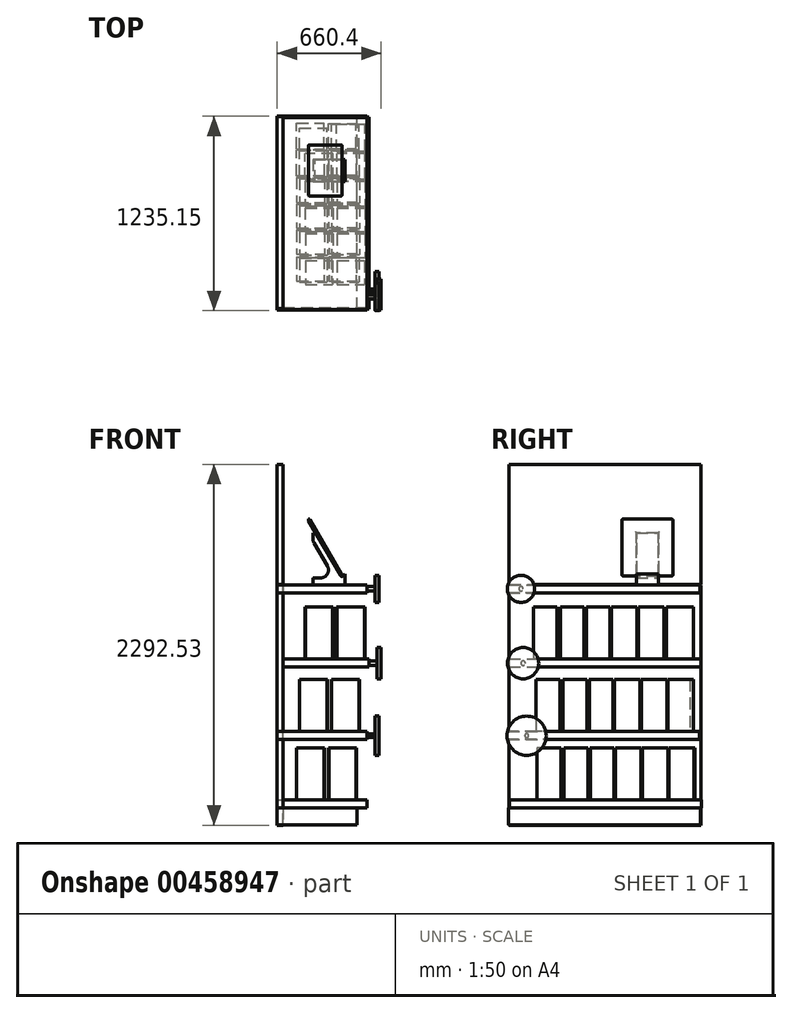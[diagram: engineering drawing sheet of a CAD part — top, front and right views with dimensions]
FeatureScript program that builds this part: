
annotation { "Feature Type Name" : "Feature", "Feature Type Description" : "" }
export const myFeature = defineFeature(function(context is Context, id is Id, definition is map)
    precondition{}
    {
        {
            var Q0;
            Q0=qCreatedBy(makeId("Right.planeOp"),FACE);
            var sketch = newSketch(context, id + "F0", { "sketchPlane" : qUnion([Q0])});
            skLineSegment(sketch, "E0.bottom", {"start": v(227.6, 704.3) * mm, "end": v(1446.8, 704.3) * mm});
            skLineSegment(sketch, "E0.top", {"start": v(227.6, -57.7) * mm, "end": v(1446.8, -57.7) * mm});
            skLineSegment(sketch, "E0.left", {"start": v(227.6, 704.3) * mm, "end": v(227.6, -57.7) * mm});
            skLineSegment(sketch, "E0.right", {"start": v(1446.8, 704.3) * mm, "end": v(1446.8, -57.7) * mm});
            skSolve(sketch);
        }
        {
            var Q0;
            Q0 = qSketchRegion(id + "F0", true);
            extrude(context, id + "F1", {"entities" : qUnion([Q0]), "depth" : 38.1 * mm, "offsetDistance" : 25.4 * mm});
        }
        {
            var Q0;
            Q0=qCreatedBy(makeId("Right.planeOp"),FACE);
            var sketch = newSketch(context, id + "F2", { "sketchPlane" : qUnion([Q0])});
            skLineSegment(sketch, "E1.bottom", {"start": v(225.61, -64.23) * mm, "end": v(1444.81, -64.23) * mm});
            skLineSegment(sketch, "E1.top", {"start": v(225.61, -1588.23) * mm, "end": v(1444.81, -1588.23) * mm});
            skLineSegment(sketch, "E1.left", {"start": v(225.61, -64.23) * mm, "end": v(225.61, -1588.23) * mm});
            skLineSegment(sketch, "E1.right", {"start": v(1444.81, -64.23) * mm, "end": v(1444.81, -1588.23) * mm});
            skSolve(sketch);
        }
        {
            var Q0;
            Q0 = qSketchRegion(id + "F2", true);
            extrude(context, id + "F3", {"entities" : qUnion([Q0]), "depth" : 38.1 * mm, "offsetDistance" : 25.4 * mm});
        }
        {
            var Q0;
            Q0=qCreatedBy(makeId("Right.planeOp"),FACE);
            var sketch = newSketch(context, id + "F4", { "sketchPlane" : qUnion([Q0])});
            skLineSegment(sketch, "E2.bottom", {"start": v(221.35, -62.55) * mm, "end": v(1440.55, -62.55) * mm});
            skLineSegment(sketch, "E2.top", {"start": v(221.35, -113.35) * mm, "end": v(1440.55, -113.35) * mm});
            skLineSegment(sketch, "E2.left", {"start": v(221.35, -62.55) * mm, "end": v(221.35, -113.35) * mm});
            skLineSegment(sketch, "E2.right", {"start": v(1440.55, -62.55) * mm, "end": v(1440.55, -113.35) * mm});
            skSolve(sketch);
        }
        {
            var Q0;
            Q0 = qSketchRegion(id + "F4", true);
            extrude(context, id + "F5", {"entities" : qUnion([Q0]), "operationType" : NewBodyOperationType.ADD, "depth" : 571.5 * mm, "offsetDistance" : 25.4 * mm});
        }
        {
            var Q0;
            Q0=makeQuery(id+"F3.opExtrude","CAP_FACE",FACE,{"disambiguationData":[OSD([sQuery(id+"F2.wireOp",EDGE,"E1.bottom"),sQuery(id+"F2.wireOp",EDGE,"E1.top"),sQuery(id+"F2.wireOp",EDGE,"E1.left"),sQuery(id+"F2.wireOp",EDGE,"E1.right")])],"isStart":false});
            var sketch = newSketch(context, id + "F6", { "sketchPlane" : qUnion([Q0])});
            skLineSegment(sketch, "E3.bottom", {"start": v(225.68, -532.06) * mm, "end": v(1444.88, -532.06) * mm});
            skLineSegment(sketch, "E3.top", {"start": v(225.68, -582.86) * mm, "end": v(1444.88, -582.86) * mm});
            skLineSegment(sketch, "E3.left", {"start": v(225.68, -532.06) * mm, "end": v(225.68, -582.86) * mm});
            skLineSegment(sketch, "E3.right", {"start": v(1444.88, -532.06) * mm, "end": v(1444.88, -582.86) * mm});
            skSolve(sketch);
        }
        {
            var Q0;
            Q0 = qSketchRegion(id + "F6", true);
            extrude(context, id + "F7", {"entities" : qUnion([Q0]), "operationType" : NewBodyOperationType.ADD, "depth" : 546.1 * mm, "offsetDistance" : 25.4 * mm});
        }
        {
            var Q0;
            Q0=qCreatedBy(makeId("Right.planeOp"),FACE);
            var sketch = newSketch(context, id + "F8", { "sketchPlane" : qUnion([Q0])});
            skLineSegment(sketch, "E4.bottom", {"start": v(218, -992.74) * mm, "end": v(1437.2, -992.74) * mm});
            skLineSegment(sketch, "E4.top", {"start": v(218, -1043.54) * mm, "end": v(1437.2, -1043.54) * mm});
            skLineSegment(sketch, "E4.left", {"start": v(218, -992.74) * mm, "end": v(218, -1043.54) * mm});
            skLineSegment(sketch, "E4.right", {"start": v(1437.2, -992.74) * mm, "end": v(1437.2, -1043.54) * mm});
            skSolve(sketch);
        }
        {
            var Q0;
            Q0 = qSketchRegion(id + "F8", true);
            var Q1;
            Q1 = qSketchRegion(id + "F4", true);
            extrude(context, id + "F9", {"entities" : qUnion([Q0, Q1]), "operationType" : NewBodyOperationType.ADD, "depth" : 571.5 * mm, "offsetDistance" : 25.4 * mm});
        }
        {
            var Q0;
            Q0=qCreatedBy(makeId("Right.planeOp"),FACE);
            var sketch = newSketch(context, id + "F10", { "sketchPlane" : qUnion([Q0])});
            skLineSegment(sketch, "E5.bottom", {"start": v(229.96, -1426.88) * mm, "end": v(1449.16, -1426.88) * mm});
            skLineSegment(sketch, "E5.top", {"start": v(229.96, -1477.68) * mm, "end": v(1449.16, -1477.68) * mm});
            skLineSegment(sketch, "E5.left", {"start": v(229.96, -1426.88) * mm, "end": v(229.96, -1477.68) * mm});
            skLineSegment(sketch, "E5.right", {"start": v(1449.16, -1426.88) * mm, "end": v(1449.16, -1477.68) * mm});
            skSolve(sketch);
        }
        {
            var Q0;
            Q0 = qSketchRegion(id + "F10", true);
            extrude(context, id + "F11", {"entities" : qUnion([Q0]), "operationType" : NewBodyOperationType.ADD, "depth" : 571.5 * mm, "offsetDistance" : 25.4 * mm});
        }
        {
            var Q0;
            Q0=qCreatedBy(makeId("Right.planeOp"),FACE);
            var sketch = newSketch(context, id + "F12", { "sketchPlane" : qUnion([Q0])});
            skLineSegment(sketch, "E6.bottom", {"start": v(222.75, -1478.96) * mm, "end": v(1441.83, -1478.96) * mm});
            skLineSegment(sketch, "E6.top", {"start": v(222.75, -1587.43) * mm, "end": v(1441.83, -1587.43) * mm});
            skLineSegment(sketch, "E6.left", {"start": v(222.75, -1478.96) * mm, "end": v(222.75, -1587.43) * mm});
            skLineSegment(sketch, "E6.right", {"start": v(1441.83, -1478.96) * mm, "end": v(1441.83, -1587.43) * mm});
            skSolve(sketch);
        }
        {
            var Q0;
            Q0 = qSketchRegion(id + "F12", true);
            extrude(context, id + "F13", {"entities" : qUnion([Q0]), "operationType" : NewBodyOperationType.ADD, "depth" : 508 * mm, "offsetDistance" : 25.4 * mm});
        }
        {
            var Q0;
            Q0=makeQuery(id+"F5.opExtrude","CAP_FACE",FACE,{"disambiguationData":[OSD([sQuery(id+"F4.wireOp",EDGE,"E2.bottom"),sQuery(id+"F4.wireOp",EDGE,"E2.top"),sQuery(id+"F4.wireOp",EDGE,"E2.left"),sQuery(id+"F4.wireOp",EDGE,"E2.right")])],"isStart":false});
            var sketch = newSketch(context, id + "F14", { "sketchPlane" : qUnion([Q0])});
            skCircle(sketch, "E7", {"center": v(302.83, -86.73) * mm, "radius": 13.67 * mm});
            skSolve(sketch);
        }
        {
            var Q0;
            Q0 = qSketchRegion(id + "F14", true);
            extrude(context, id + "F15", {"entities" : qUnion([Q0]), "operationType" : NewBodyOperationType.ADD, "depth" : 50.8 * mm, "offsetDistance" : 25.4 * mm});
        }
        {
            var Q0;
            Q0=makeQuery(id+"F15.opExtrude","CAP_FACE",FACE,{"disambiguationData":[OSD([sQuery(id+"F14.wireOp",EDGE,"E7")])],"isStart":false});
            var sketch = newSketch(context, id + "F16", { "sketchPlane" : qUnion([Q0])});
            skCircle(sketch, "E8", {"center": v(302.83, -86.73) * mm, "radius": 86.26 * mm});
            skSolve(sketch);
        }
        {
            var Q0;
            Q0 = qSketchRegion(id + "F16", true);
            extrude(context, id + "F17", {"entities" : qUnion([Q0]), "operationType" : NewBodyOperationType.ADD, "depth" : 25.4 * mm, "offsetDistance" : 25.4 * mm});
        }
        {
            var Q0;
            Q0=makeQuery(id+"F7.opExtrude","CAP_FACE",FACE,{"disambiguationData":[OSD([sQuery(id+"F6.wireOp",EDGE,"E3.bottom"),sQuery(id+"F6.wireOp",EDGE,"E3.top"),sQuery(id+"F6.wireOp",EDGE,"E3.left"),sQuery(id+"F6.wireOp",EDGE,"E3.right")])],"isStart":false});
            var sketch = newSketch(context, id + "F18", { "sketchPlane" : qUnion([Q0])});
            skCircle(sketch, "E9", {"center": v(316.35, -559.4) * mm, "radius": 13.67 * mm});
            skSolve(sketch);
        }
        {
            var Q0;
            Q0=makeQuery(id+"F5.opExtrude","SWEPT_FACE",FACE,{"disambiguationData":[OSD([sQuery(id+"F4.wireOp",EDGE,"E2.bottom")])]});
            var sketch = newSketch(context, id + "F19", { "sketchPlane" : qUnion([Q0])});
            skLineSegment(sketch, "E10.bottom", {"start": v(226.95, 1175) * mm, "end": v(432.13, 1175) * mm});
            skLineSegment(sketch, "E10.top", {"start": v(226.95, 1034.88) * mm, "end": v(432.13, 1034.88) * mm});
            skLineSegment(sketch, "E10.left", {"start": v(226.95, 1175) * mm, "end": v(226.95, 1034.88) * mm});
            skLineSegment(sketch, "E10.right", {"start": v(432.13, 1175) * mm, "end": v(432.13, 1034.88) * mm});
            skSolve(sketch);
        }
        {
            var Q0;
            Q0 = qSketchRegion(id + "F19", true);
            extrude(context, id + "F20", {"entities" : qUnion([Q0]), "operationType" : NewBodyOperationType.ADD, "depth" : 330.2 * mm, "offsetDistance" : 25.4 * mm});
        }
        {
            var Q0;
            Q0=makeQuery(id+"F20.opExtrude","SWEPT_FACE",FACE,{"disambiguationData":[OSD([sQuery(id+"F19.wireOp",EDGE,"E10.bottom")])]});
            var sketch = newSketch(context, id + "F21", { "sketchPlane" : qUnion([Q0])});
            skLineSegment(sketch, "E11", {"start": v(-432.13, 7.23) * mm, "end": v(-408.06, -11.66) * mm});
            skLineSegment(sketch, "E12", {"start": v(-408.06, -11.66) * mm, "end": v(-156.77, 419.01) * mm});
            skLineSegment(sketch, "E13", {"start": v(-156.77, 419.01) * mm, "end": v(-699.03, 419.01) * mm});
            skLineSegment(sketch, "E14", {"start": v(-699.03, 419.01) * mm, "end": v(-432.13, 7.23) * mm});
            skSolve(sketch);
        }
        {
            var Q0;
            Q0 = qSketchRegion(id + "F21", true);
            extrude(context, id + "F22", {"entities" : qUnion([Q0]), "operationType" : NewBodyOperationType.REMOVE, "endBound" : BoundingType.THROUGH_ALL, "oppositeDirection" : true, "depth" : 25.4 * mm, "offsetDistance" : 25.4 * mm});
        }
        {
            var Q0;
            Q0=makeQuery(id+"F20.opExtrude","SWEPT_FACE",FACE,{"disambiguationData":[OSD([sQuery(id+"F19.wireOp",EDGE,"E10.bottom")])]});
            var sketch = newSketch(context, id + "F23", { "sketchPlane" : qUnion([Q0])});
            skLineSegment(sketch, "E15", {"start": v(-172.97, 309.72) * mm, "end": v(-363.93, -17.56) * mm});
            skLineSegment(sketch, "E16", {"start": v(-363.93, -17.56) * mm, "end": v(-141.24, -17.56) * mm});
            skLineSegment(sketch, "E17", {"start": v(-141.24, -17.56) * mm, "end": v(-172.97, 309.72) * mm});
            skSolve(sketch);
        }
        {
            var Q0;
            Q0 = qSketchRegion(id + "F23", true);
            extrude(context, id + "F24", {"entities" : qUnion([Q0]), "operationType" : NewBodyOperationType.REMOVE, "endBound" : BoundingType.THROUGH_ALL, "oppositeDirection" : true, "depth" : 25.4 * mm, "offsetDistance" : 25.4 * mm});
        }
        {
            var Q0;
            Q0=makeQuery(id+"F24.boolean.opBoolean","COPY",EDGE,{"derivedFrom":makeQuery(id+"F24.opExtrude","SWEPT_EDGE",EDGE,{"disambiguationData":[OSD([sQuery(id+"F23.wireOp",EDGE,"E15"),sQuery(id+"F23.wireOp",EDGE,"E16")])]})});
            fillet(context, id + "F25", {"entities" : qUnion([Q0]), "radius" : 50.8 * mm, "tangentPropagation" : true, "allowEdgeOverflow" : false});
        }
        {
            var Q0;
            Q0=makeQuery(id+"F24.boolean.opBoolean","INTERSECT",EDGE,{"derivedFrom":[makeQuery(id+"F20.opExtrude","SWEPT_FACE",FACE,{"disambiguationData":[OSD([sQuery(id+"F19.wireOp",EDGE,"E10.left")])]}),makeQuery(id+"F24.opExtrude","SWEPT_FACE",FACE,{"disambiguationData":[OSD([sQuery(id+"F23.wireOp",EDGE,"E15")])]})]});
            fillet(context, id + "F26", {"entities" : qUnion([Q0]), "radius" : 50.8 * mm, "tangentPropagation" : true, "allowEdgeOverflow" : false});
        }
        {
            var Q0;
            Q0=makeQuery(id+"F22.boolean.opBoolean","INTERSECT",EDGE,{"derivedFrom":[makeQuery(id+"F20.opExtrude","CAP_FACE",FACE,{"disambiguationData":[OSD([sQuery(id+"F19.wireOp",EDGE,"E10.bottom"),sQuery(id+"F19.wireOp",EDGE,"E10.top"),sQuery(id+"F19.wireOp",EDGE,"E10.left"),sQuery(id+"F19.wireOp",EDGE,"E10.right")])],"isStart":false}),makeQuery(id+"F22.opExtrude","SWEPT_FACE",FACE,{"disambiguationData":[OSD([sQuery(id+"F21.wireOp",EDGE,"E12")])]})]});
            fillet(context, id + "F27", {"entities" : qUnion([Q0]), "radius" : 25.4 * mm, "tangentPropagation" : true, "allowEdgeOverflow" : false});
        }
        {
            var Q0;
            Q0=makeQuery(id+"F22.boolean.opBoolean","COPY",EDGE,{"derivedFrom":makeQuery(id+"F22.opExtrude","SWEPT_EDGE",EDGE,{"disambiguationData":[OSD([sQuery(id+"F21.wireOp",EDGE,"E11"),sQuery(id+"F21.wireOp",EDGE,"E12")])]})});
            var Q1;
            Q1=makeQuery(id+"F22.boolean.opBoolean","COPY",EDGE,{"derivedFrom":makeQuery(id+"F22.opExtrude","SWEPT_EDGE",EDGE,{"disambiguationData":[OSD([sQuery(id+"F19.wireOp",EDGE,"E10.bottom"),sQuery(id+"F19.wireOp",EDGE,"E10.right"),sQuery(id+"F21.wireOp",EDGE,"E11"),sQuery(id+"F21.wireOp",EDGE,"E14")])]})});
            var Q2;
            Q2=makeQuery(id+"F24.boolean.opBoolean","INTERSECT",EDGE,{"derivedFrom":[makeQuery(id+"F20.opExtrude","SWEPT_FACE",FACE,{"disambiguationData":[OSD([sQuery(id+"F19.wireOp",EDGE,"E10.left")])]}),makeQuery(id+"F24.opExtrude","SWEPT_FACE",FACE,{"disambiguationData":[OSD([sQuery(id+"F23.wireOp",EDGE,"E16")])]})]});
            fillet(context, id + "F28", {"entities" : qUnion([Q0, Q1, Q2]), "radius" : 5.08 * mm, "tangentPropagation" : true, "allowEdgeOverflow" : false});
        }
        {
            var Q0;
            Q0=makeQuery(id+"F22.boolean.opBoolean","COPY",FACE,{"derivedFrom":makeQuery(id+"F22.opExtrude","SWEPT_FACE",FACE,{"disambiguationData":[OSD([sQuery(id+"F21.wireOp",EDGE,"E12")])]})});
            var sketch = newSketch(context, id + "F29", { "sketchPlane" : qUnion([Q0])});
            skLineSegment(sketch, "E18.bottom", {"start": v(942.43, 205.9) * mm, "end": v(1267.72, 205.9) * mm});
            skLineSegment(sketch, "E18.top", {"start": v(942.43, -211.28) * mm, "end": v(1267.72, -211.28) * mm});
            skLineSegment(sketch, "E18.left", {"start": v(942.43, 205.9) * mm, "end": v(942.43, -211.28) * mm});
            skLineSegment(sketch, "E18.right", {"start": v(1267.72, 205.9) * mm, "end": v(1267.72, -211.28) * mm});
            skSolve(sketch);
        }
        {
            var Q0;
            Q0 = qSketchRegion(id + "F29", true);
            extrude(context, id + "F30", {"entities" : qUnion([Q0]), "operationType" : NewBodyOperationType.ADD, "depth" : 8.9 * mm, "offsetDistance" : 25.4 * mm});
        }
        {
            var Q0;
            Q0=makeQuery(id+"F30.opExtrude","SWEPT_EDGE",EDGE,{"disambiguationData":[OSD([sQuery(id+"F29.wireOp",EDGE,"E18.bottom"),sQuery(id+"F29.wireOp",EDGE,"E18.right")])]});
            var Q1;
            Q1=makeQuery(id+"F30.opExtrude","SWEPT_EDGE",EDGE,{"disambiguationData":[OSD([sQuery(id+"F29.wireOp",EDGE,"E18.top"),sQuery(id+"F29.wireOp",EDGE,"E18.right")])]});
            var Q2;
            Q2=makeQuery(id+"F30.opExtrude","SWEPT_EDGE",EDGE,{"disambiguationData":[OSD([sQuery(id+"F29.wireOp",EDGE,"E18.top"),sQuery(id+"F29.wireOp",EDGE,"E18.left")])]});
            var Q3;
            Q3=makeQuery(id+"F30.opExtrude","SWEPT_EDGE",EDGE,{"disambiguationData":[OSD([sQuery(id+"F29.wireOp",EDGE,"E18.bottom"),sQuery(id+"F29.wireOp",EDGE,"E18.left")])]});
            fillet(context, id + "F31", {"entities" : qUnion([Q0, Q1, Q2, Q3]), "radius" : 8.9 * mm, "tangentPropagation" : true, "allowEdgeOverflow" : false});
        }
        {
            var Q0;
            Q0=makeQuery(id+"F30.opExtrude","CAP_FACE",FACE,{"disambiguationData":[OSD([sQuery(id+"F29.wireOp",EDGE,"E18.bottom"),sQuery(id+"F29.wireOp",EDGE,"E18.top"),sQuery(id+"F29.wireOp",EDGE,"E18.left"),sQuery(id+"F29.wireOp",EDGE,"E18.right")])],"isStart":true});
            fillet(context, id + "F32", {"entities" : qUnion([Q0]), "radius" : 6.35 * mm, "allowEdgeOverflow" : false});
        }
        {
            var Q0;
            Q0=makeQuery(id+"F30.opExtrude","CAP_EDGE",EDGE,{"disambiguationData":[OSD([sQuery(id+"F29.wireOp",EDGE,"E18.left")])],"isStart":false});
            var Q1;
            Q1=makeQuery(id+"F30.opExtrude","CAP_EDGE",EDGE,{"disambiguationData":[OSD([sQuery(id+"F29.wireOp",EDGE,"E18.bottom")])],"isStart":false});
            var Q2;
            {var subQ0=sQuery(id+"F29.wireOp",EDGE,"E18.left");var subQ1=sQuery(id+"F29.wireOp",EDGE,"E18.bottom");Q2=makeQuery(id+"F31.opFillet","BLEND_EDGE",EDGE,{"blendedFrom":[makeQuery(id+"F30.opExtrude","SWEPT_EDGE",EDGE,{"disambiguationData":[OSD([subQ1,subQ0])]}),makeQuery(id+"F30.opExtrude","CAP_FACE",FACE,{"disambiguationData":[OSD([subQ1,sQuery(id+"F29.wireOp",EDGE,"E18.top"),subQ0,sQuery(id+"F29.wireOp",EDGE,"E18.right")])],"isStart":false})],"blendedInto":[makeQuery(id+"F30.opExtrude","CAP_FACE",FACE,{"disambiguationData":[OSD([subQ1,sQuery(id+"F29.wireOp",EDGE,"E18.top"),subQ0,sQuery(id+"F29.wireOp",EDGE,"E18.right")])],"isStart":false})]});}
            var Q3;
            {var subQ0=sQuery(id+"F29.wireOp",EDGE,"E18.right");var subQ1=sQuery(id+"F29.wireOp",EDGE,"E18.bottom");Q3=makeQuery(id+"F31.opFillet","BLEND_EDGE",EDGE,{"blendedFrom":[makeQuery(id+"F30.opExtrude","SWEPT_EDGE",EDGE,{"disambiguationData":[OSD([subQ1,subQ0])]}),makeQuery(id+"F30.opExtrude","CAP_FACE",FACE,{"disambiguationData":[OSD([subQ1,sQuery(id+"F29.wireOp",EDGE,"E18.top"),sQuery(id+"F29.wireOp",EDGE,"E18.left"),subQ0])],"isStart":false})],"blendedInto":[makeQuery(id+"F30.opExtrude","CAP_FACE",FACE,{"disambiguationData":[OSD([subQ1,sQuery(id+"F29.wireOp",EDGE,"E18.top"),sQuery(id+"F29.wireOp",EDGE,"E18.left"),subQ0])],"isStart":false})]});}
            var Q4;
            Q4=makeQuery(id+"F30.opExtrude","CAP_EDGE",EDGE,{"disambiguationData":[OSD([sQuery(id+"F29.wireOp",EDGE,"E18.right")])],"isStart":false});
            fillet(context, id + "F33", {"entities" : qUnion([Q0, Q1, Q2, Q3, Q4]), "radius" : 2.54 * mm, "tangentPropagation" : true, "allowEdgeOverflow" : false});
        }
        {
            var Q0;
            Q0 = qSketchRegion(id + "F18", true);
            extrude(context, id + "F34", {"entities" : qUnion([Q0]), "operationType" : NewBodyOperationType.ADD, "depth" : 50.8 * mm, "offsetDistance" : 25.4 * mm});
        }
        {
            var Q0;
            Q0=makeQuery(id+"F34.opExtrude","CAP_FACE",FACE,{"disambiguationData":[OSD([sQuery(id+"F18.wireOp",EDGE,"E9")])],"isStart":false});
            var sketch = newSketch(context, id + "F35", { "sketchPlane" : qUnion([Q0])});
            skCircle(sketch, "E19", {"center": v(316.35, -559.4) * mm, "radius": 99.15 * mm});
            skSolve(sketch);
        }
        {
            var Q0;
            Q0 = qSketchRegion(id + "F35", true);
            extrude(context, id + "F36", {"entities" : qUnion([Q0]), "operationType" : NewBodyOperationType.ADD, "depth" : 25.4 * mm, "offsetDistance" : 25.4 * mm});
        }
        {
            var Q0;
            Q0=makeQuery(id+"F9.opExtrude","CAP_FACE",FACE,{"disambiguationData":[OSD([sQuery(id+"F8.wireOp",EDGE,"E4.bottom"),sQuery(id+"F8.wireOp",EDGE,"E4.top"),sQuery(id+"F8.wireOp",EDGE,"E4.left"),sQuery(id+"F8.wireOp",EDGE,"E4.right")])],"isStart":false});
            var sketch = newSketch(context, id + "F37", { "sketchPlane" : qUnion([Q0])});
            skCircle(sketch, "E20", {"center": v(338.35, -1019.78) * mm, "radius": 12.3 * mm});
            skSolve(sketch);
        }
        {
            var Q0;
            Q0 = qSketchRegion(id + "F37", true);
            extrude(context, id + "F38", {"entities" : qUnion([Q0]), "operationType" : NewBodyOperationType.ADD, "depth" : 50.8 * mm, "offsetDistance" : 25.4 * mm});
        }
        {
            var Q0;
            Q0=makeQuery(id+"F38.opExtrude","CAP_FACE",FACE,{"disambiguationData":[OSD([sQuery(id+"F37.wireOp",EDGE,"E20")])],"isStart":false});
            var sketch = newSketch(context, id + "F39", { "sketchPlane" : qUnion([Q0])});
            skCircle(sketch, "E21", {"center": v(338.35, -1019.78) * mm, "radius": 124.34 * mm});
            skSolve(sketch);
        }
        {
            var Q0;
            Q0 = qSketchRegion(id + "F39", true);
            extrude(context, id + "F40", {"entities" : qUnion([Q0]), "operationType" : NewBodyOperationType.ADD, "depth" : 25.4 * mm, "offsetDistance" : 25.4 * mm});
        }
        {
            var Q0;
            Q0=makeQuery(id+"F7.opExtrude","SWEPT_FACE",FACE,{"disambiguationData":[OSD([sQuery(id+"F6.wireOp",EDGE,"E3.bottom")])]});
            var sketch = newSketch(context, id + "F41", { "sketchPlane" : qUnion([Q0])});
            skLineSegment(sketch, "E22.bottom", {"start": v(557.55, 1225.5) * mm, "end": v(378.5, 1225.5) * mm});
            skLineSegment(sketch, "E22.top", {"start": v(557.55, 1397.6) * mm, "end": v(378.5, 1397.6) * mm});
            skLineSegment(sketch, "E22.left", {"start": v(557.55, 1225.5) * mm, "end": v(557.55, 1397.6) * mm});
            skLineSegment(sketch, "E22.right", {"start": v(378.5, 1225.5) * mm, "end": v(378.5, 1397.6) * mm});
            skSolve(sketch);
        }
        {
            var Q0;
            Q0 = qSketchRegion(id + "F41", true);
            extrude(context, id + "F42", {"entities" : qUnion([Q0]), "operationType" : NewBodyOperationType.ADD, "depth" : 330.2 * mm, "offsetDistance" : 25.4 * mm});
        }
        {
            var Q0;
            Q0=makeQuery(id+"F7.opExtrude","SWEPT_FACE",FACE,{"disambiguationData":[OSD([sQuery(id+"F6.wireOp",EDGE,"E3.bottom")])]});
            var sketch = newSketch(context, id + "F43", { "sketchPlane" : qUnion([Q0])});
            skLineSegment(sketch, "E23.bottom", {"start": v(557.55, 1047.5) * mm, "end": v(379.45, 1047.5) * mm});
            skLineSegment(sketch, "E23.top", {"start": v(557.55, 1211.23) * mm, "end": v(379.45, 1211.23) * mm});
            skLineSegment(sketch, "E23.left", {"start": v(557.55, 1047.5) * mm, "end": v(557.55, 1211.23) * mm});
            skLineSegment(sketch, "E23.right", {"start": v(379.45, 1047.5) * mm, "end": v(379.45, 1211.23) * mm});
            skLineSegment(sketch, "E24.bottom", {"start": v(379.45, 1038.12) * mm, "end": v(556.57, 1038.12) * mm});
            skLineSegment(sketch, "E24.top", {"start": v(379.45, 878.23) * mm, "end": v(556.57, 878.23) * mm});
            skLineSegment(sketch, "E24.left", {"start": v(379.45, 1038.12) * mm, "end": v(379.45, 878.23) * mm});
            skLineSegment(sketch, "E24.right", {"start": v(556.57, 1038.12) * mm, "end": v(556.57, 878.23) * mm});
            skLineSegment(sketch, "E25.bottom", {"start": v(379.45, 867.5) * mm, "end": v(556.57, 867.5) * mm});
            skLineSegment(sketch, "E25.top", {"start": v(379.45, 718.09) * mm, "end": v(556.57, 718.09) * mm});
            skLineSegment(sketch, "E25.left", {"start": v(379.45, 867.5) * mm, "end": v(379.45, 718.09) * mm});
            skLineSegment(sketch, "E25.right", {"start": v(556.57, 867.5) * mm, "end": v(556.57, 718.09) * mm});
            skLineSegment(sketch, "E26.bottom", {"start": v(380.2, 702.92) * mm, "end": v(557.25, 702.92) * mm});
            skLineSegment(sketch, "E26.top", {"start": v(380.2, 551.6) * mm, "end": v(557.25, 551.6) * mm});
            skLineSegment(sketch, "E26.left", {"start": v(380.2, 702.92) * mm, "end": v(380.2, 551.6) * mm});
            skLineSegment(sketch, "E26.right", {"start": v(557.25, 702.92) * mm, "end": v(557.25, 551.6) * mm});
            skLineSegment(sketch, "E27.bottom", {"start": v(380.2, 532.48) * mm, "end": v(554.24, 532.48) * mm});
            skLineSegment(sketch, "E27.top", {"start": v(380.2, 380.99) * mm, "end": v(554.24, 380.99) * mm});
            skLineSegment(sketch, "E27.left", {"start": v(380.2, 532.48) * mm, "end": v(380.2, 380.99) * mm});
            skLineSegment(sketch, "E27.right", {"start": v(554.24, 532.48) * mm, "end": v(554.24, 380.99) * mm});
            skLineSegment(sketch, "E28.left", {"start": v(150.85, 1064.42) * mm, "end": v(150.85, 1228.16) * mm});
            skLineSegment(sketch, "E29.bottom", {"start": v(356.13, 1047.5) * mm, "end": v(178.04, 1047.5) * mm});
            skLineSegment(sketch, "E29.top", {"start": v(356.13, 1211.23) * mm, "end": v(178.04, 1211.23) * mm});
            skLineSegment(sketch, "E29.left", {"start": v(356.13, 1047.5) * mm, "end": v(356.13, 1211.23) * mm});
            skLineSegment(sketch, "E29.right", {"start": v(178.04, 1047.5) * mm, "end": v(178.04, 1211.23) * mm});
            skLineSegment(sketch, "E30.bottom", {"start": v(178.04, 1038.12) * mm, "end": v(355.16, 1038.12) * mm});
            skLineSegment(sketch, "E30.top", {"start": v(178.04, 878.23) * mm, "end": v(355.16, 878.23) * mm});
            skLineSegment(sketch, "E30.left", {"start": v(178.04, 1038.12) * mm, "end": v(178.04, 878.23) * mm});
            skLineSegment(sketch, "E30.right", {"start": v(355.16, 1038.12) * mm, "end": v(355.16, 878.23) * mm});
            skLineSegment(sketch, "E31.bottom", {"start": v(178.04, 867.5) * mm, "end": v(355.16, 867.5) * mm});
            skLineSegment(sketch, "E31.top", {"start": v(178.04, 718.09) * mm, "end": v(355.16, 718.09) * mm});
            skLineSegment(sketch, "E31.left", {"start": v(178.04, 867.5) * mm, "end": v(178.04, 718.09) * mm});
            skLineSegment(sketch, "E31.right", {"start": v(355.16, 867.5) * mm, "end": v(355.16, 718.09) * mm});
            skLineSegment(sketch, "E32.bottom", {"start": v(178.79, 702.92) * mm, "end": v(355.84, 702.92) * mm});
            skLineSegment(sketch, "E32.top", {"start": v(178.79, 551.6) * mm, "end": v(355.84, 551.6) * mm});
            skLineSegment(sketch, "E32.left", {"start": v(178.79, 702.92) * mm, "end": v(178.79, 551.6) * mm});
            skLineSegment(sketch, "E32.right", {"start": v(355.84, 702.92) * mm, "end": v(355.84, 551.6) * mm});
            skLineSegment(sketch, "E33.bottom", {"start": v(178.79, 532.48) * mm, "end": v(352.83, 532.48) * mm});
            skLineSegment(sketch, "E33.top", {"start": v(178.79, 380.99) * mm, "end": v(352.83, 380.99) * mm});
            skLineSegment(sketch, "E33.left", {"start": v(178.79, 532.48) * mm, "end": v(178.79, 380.99) * mm});
            skLineSegment(sketch, "E33.right", {"start": v(352.83, 532.48) * mm, "end": v(352.83, 380.99) * mm});
            skSolve(sketch);
        }
        {
            var Q0;
            Q0 = qSketchRegion(id + "F43", true);
            extrude(context, id + "F44", {"entities" : qUnion([Q0]), "operationType" : NewBodyOperationType.ADD, "depth" : 330.2 * mm, "offsetDistance" : 25.4 * mm});
        }
        {
            var Q0;
            Q0 = qSketchRegion(id + "F43", true);
            extrude(context, id + "F45", {"entities" : qUnion([Q0]), "operationType" : NewBodyOperationType.ADD, "depth" : 330.2 * mm, "offsetDistance" : 25.4 * mm});
        }
        {
            var Q0;
            Q0=makeQuery(id+"F9.opExtrude","SWEPT_FACE",FACE,{"disambiguationData":[OSD([sQuery(id+"F8.wireOp",EDGE,"E4.bottom")])]});
            var sketch = newSketch(context, id + "F46", { "sketchPlane" : qUnion([Q0])});
            skLineSegment(sketch, "E34.bottom", {"start": v(523.1, 1065.98) * mm, "end": v(345, 1065.98) * mm});
            skLineSegment(sketch, "E34.top", {"start": v(523.1, 1229.72) * mm, "end": v(345, 1229.72) * mm});
            skLineSegment(sketch, "E34.left", {"start": v(523.1, 1065.98) * mm, "end": v(523.1, 1229.72) * mm});
            skLineSegment(sketch, "E34.right", {"start": v(345, 1065.98) * mm, "end": v(345, 1229.72) * mm});
            skLineSegment(sketch, "E35.bottom", {"start": v(345, 1056.61) * mm, "end": v(522.12, 1056.61) * mm});
            skLineSegment(sketch, "E35.top", {"start": v(345, 896.72) * mm, "end": v(522.12, 896.72) * mm});
            skLineSegment(sketch, "E35.left", {"start": v(345, 1056.61) * mm, "end": v(345, 896.72) * mm});
            skLineSegment(sketch, "E35.right", {"start": v(522.12, 1056.61) * mm, "end": v(522.12, 896.72) * mm});
            skLineSegment(sketch, "E36.bottom", {"start": v(345, 885.98) * mm, "end": v(522.12, 885.98) * mm});
            skLineSegment(sketch, "E36.top", {"start": v(345, 736.58) * mm, "end": v(522.12, 736.58) * mm});
            skLineSegment(sketch, "E36.left", {"start": v(345, 885.98) * mm, "end": v(345, 736.58) * mm});
            skLineSegment(sketch, "E36.right", {"start": v(522.12, 885.98) * mm, "end": v(522.12, 736.58) * mm});
            skLineSegment(sketch, "E37.bottom", {"start": v(345.75, 721.41) * mm, "end": v(522.8, 721.41) * mm});
            skLineSegment(sketch, "E37.top", {"start": v(345.75, 570.1) * mm, "end": v(522.8, 570.1) * mm});
            skLineSegment(sketch, "E37.left", {"start": v(345.75, 721.41) * mm, "end": v(345.75, 570.1) * mm});
            skLineSegment(sketch, "E37.right", {"start": v(522.8, 721.41) * mm, "end": v(522.8, 570.1) * mm});
            skLineSegment(sketch, "E38.bottom", {"start": v(345.75, 550.97) * mm, "end": v(519.8, 550.97) * mm});
            skLineSegment(sketch, "E38.top", {"start": v(345.75, 397.33) * mm, "end": v(519.8, 397.33) * mm});
            skLineSegment(sketch, "E38.left", {"start": v(345.75, 550.97) * mm, "end": v(345.75, 397.33) * mm});
            skLineSegment(sketch, "E38.right", {"start": v(519.8, 550.97) * mm, "end": v(519.8, 397.33) * mm});
            skLineSegment(sketch, "E39.bottom", {"start": v(345, 1236.38) * mm, "end": v(519.41, 1236.38) * mm});
            skLineSegment(sketch, "E39.top", {"start": v(345, 1398.94) * mm, "end": v(519.41, 1398.94) * mm});
            skLineSegment(sketch, "E39.left", {"start": v(345, 1236.38) * mm, "end": v(345, 1398.94) * mm});
            skLineSegment(sketch, "E39.right", {"start": v(519.41, 1236.38) * mm, "end": v(519.41, 1398.94) * mm});
            skLineSegment(sketch, "E40.bottom", {"start": v(319.23, 1063.84) * mm, "end": v(141.14, 1063.84) * mm});
            skLineSegment(sketch, "E40.top", {"start": v(319.23, 1227.57) * mm, "end": v(141.14, 1227.57) * mm});
            skLineSegment(sketch, "E40.left", {"start": v(319.23, 1063.84) * mm, "end": v(319.23, 1227.57) * mm});
            skLineSegment(sketch, "E40.right", {"start": v(141.14, 1063.84) * mm, "end": v(141.14, 1227.57) * mm});
            skLineSegment(sketch, "E41.bottom", {"start": v(141.14, 1054.47) * mm, "end": v(318.26, 1054.47) * mm});
            skLineSegment(sketch, "E41.top", {"start": v(141.14, 894.58) * mm, "end": v(318.26, 894.58) * mm});
            skLineSegment(sketch, "E41.left", {"start": v(141.14, 1054.47) * mm, "end": v(141.14, 894.58) * mm});
            skLineSegment(sketch, "E41.right", {"start": v(318.26, 1054.47) * mm, "end": v(318.26, 894.58) * mm});
            skLineSegment(sketch, "E42.bottom", {"start": v(141.14, 883.84) * mm, "end": v(318.26, 883.84) * mm});
            skLineSegment(sketch, "E42.top", {"start": v(141.14, 734.43) * mm, "end": v(318.26, 734.43) * mm});
            skLineSegment(sketch, "E42.left", {"start": v(141.14, 883.84) * mm, "end": v(141.14, 734.43) * mm});
            skLineSegment(sketch, "E42.right", {"start": v(318.26, 883.84) * mm, "end": v(318.26, 734.43) * mm});
            skLineSegment(sketch, "E43.bottom", {"start": v(141.89, 719.27) * mm, "end": v(318.94, 719.27) * mm});
            skLineSegment(sketch, "E43.top", {"start": v(141.89, 567.94) * mm, "end": v(318.94, 567.94) * mm});
            skLineSegment(sketch, "E43.left", {"start": v(141.89, 719.27) * mm, "end": v(141.89, 567.94) * mm});
            skLineSegment(sketch, "E43.right", {"start": v(318.94, 719.27) * mm, "end": v(318.94, 567.94) * mm});
            skLineSegment(sketch, "E44.bottom", {"start": v(141.89, 548.83) * mm, "end": v(315.93, 548.83) * mm});
            skLineSegment(sketch, "E44.top", {"start": v(141.89, 397.33) * mm, "end": v(315.93, 397.33) * mm});
            skLineSegment(sketch, "E44.left", {"start": v(141.89, 548.83) * mm, "end": v(141.89, 397.33) * mm});
            skLineSegment(sketch, "E44.right", {"start": v(315.93, 548.83) * mm, "end": v(315.93, 397.33) * mm});
            skLineSegment(sketch, "E45.bottom", {"start": v(141.14, 1234.23) * mm, "end": v(315.55, 1234.23) * mm});
            skLineSegment(sketch, "E45.top", {"start": v(141.14, 1374.98) * mm, "end": v(315.55, 1374.98) * mm});
            skLineSegment(sketch, "E45.left", {"start": v(141.14, 1234.23) * mm, "end": v(141.14, 1374.98) * mm});
            skLineSegment(sketch, "E45.right", {"start": v(315.55, 1234.23) * mm, "end": v(315.55, 1374.98) * mm});
            skSolve(sketch);
        }
        {
            var Q0;
            Q0 = qSketchRegion(id + "F46", true);
            extrude(context, id + "F47", {"entities" : qUnion([Q0]), "operationType" : NewBodyOperationType.ADD, "depth" : 330.2 * mm, "offsetDistance" : 25.4 * mm});
        }
        {
            var Q0;
            Q0=makeQuery(id+"F11.opExtrude","SWEPT_FACE",FACE,{"disambiguationData":[OSD([sQuery(id+"F10.wireOp",EDGE,"E5.bottom")])]});
            var sketch = newSketch(context, id + "F48", { "sketchPlane" : qUnion([Q0])});
            skLineSegment(sketch, "E46.bottom", {"start": v(505.42, 1072.46) * mm, "end": v(327.32, 1072.46) * mm});
            skLineSegment(sketch, "E46.top", {"start": v(505.42, 1236.2) * mm, "end": v(327.32, 1236.2) * mm});
            skLineSegment(sketch, "E46.left", {"start": v(505.42, 1072.46) * mm, "end": v(505.42, 1236.2) * mm});
            skLineSegment(sketch, "E46.right", {"start": v(327.32, 1072.46) * mm, "end": v(327.32, 1236.2) * mm});
            skLineSegment(sketch, "E47.bottom", {"start": v(327.32, 1063.09) * mm, "end": v(504.44, 1063.09) * mm});
            skLineSegment(sketch, "E47.top", {"start": v(327.32, 903.2) * mm, "end": v(504.44, 903.2) * mm});
            skLineSegment(sketch, "E47.left", {"start": v(327.32, 1063.09) * mm, "end": v(327.32, 903.2) * mm});
            skLineSegment(sketch, "E47.right", {"start": v(504.44, 1063.09) * mm, "end": v(504.44, 903.2) * mm});
            skLineSegment(sketch, "E48.bottom", {"start": v(327.32, 892.46) * mm, "end": v(504.44, 892.46) * mm});
            skLineSegment(sketch, "E48.top", {"start": v(327.32, 743.06) * mm, "end": v(504.44, 743.06) * mm});
            skLineSegment(sketch, "E48.left", {"start": v(327.32, 892.46) * mm, "end": v(327.32, 743.06) * mm});
            skLineSegment(sketch, "E48.right", {"start": v(504.44, 892.46) * mm, "end": v(504.44, 743.06) * mm});
            skLineSegment(sketch, "E49.bottom", {"start": v(328.07, 727.9) * mm, "end": v(505.12, 727.9) * mm});
            skLineSegment(sketch, "E49.top", {"start": v(328.07, 576.57) * mm, "end": v(505.12, 576.57) * mm});
            skLineSegment(sketch, "E49.left", {"start": v(328.07, 727.9) * mm, "end": v(328.07, 576.57) * mm});
            skLineSegment(sketch, "E49.right", {"start": v(505.12, 727.9) * mm, "end": v(505.12, 576.57) * mm});
            skLineSegment(sketch, "E50.bottom", {"start": v(328.07, 557.45) * mm, "end": v(502.11, 557.45) * mm});
            skLineSegment(sketch, "E50.top", {"start": v(328.07, 403.8) * mm, "end": v(502.11, 403.8) * mm});
            skLineSegment(sketch, "E50.left", {"start": v(328.07, 557.45) * mm, "end": v(328.07, 403.8) * mm});
            skLineSegment(sketch, "E50.right", {"start": v(502.11, 557.45) * mm, "end": v(502.11, 403.8) * mm});
            skLineSegment(sketch, "E51.bottom", {"start": v(327.32, 1242.85) * mm, "end": v(501.73, 1242.85) * mm});
            skLineSegment(sketch, "E51.top", {"start": v(327.32, 1402.43) * mm, "end": v(501.73, 1402.43) * mm});
            skLineSegment(sketch, "E51.left", {"start": v(327.32, 1242.85) * mm, "end": v(327.32, 1402.43) * mm});
            skLineSegment(sketch, "E51.right", {"start": v(501.73, 1242.85) * mm, "end": v(501.73, 1402.43) * mm});
            skLineSegment(sketch, "E52.bottom", {"start": v(301.55, 1070.32) * mm, "end": v(123.45, 1070.32) * mm});
            skLineSegment(sketch, "E52.top", {"start": v(301.55, 1234.05) * mm, "end": v(123.45, 1234.05) * mm});
            skLineSegment(sketch, "E52.left", {"start": v(301.55, 1070.32) * mm, "end": v(301.55, 1234.05) * mm});
            skLineSegment(sketch, "E52.right", {"start": v(123.45, 1070.32) * mm, "end": v(123.45, 1234.05) * mm});
            skLineSegment(sketch, "E53.bottom", {"start": v(123.45, 1060.94) * mm, "end": v(300.57, 1060.94) * mm});
            skLineSegment(sketch, "E53.top", {"start": v(123.45, 901.05) * mm, "end": v(300.57, 901.05) * mm});
            skLineSegment(sketch, "E53.left", {"start": v(123.45, 1060.94) * mm, "end": v(123.45, 901.05) * mm});
            skLineSegment(sketch, "E53.right", {"start": v(300.57, 1060.94) * mm, "end": v(300.57, 901.05) * mm});
            skLineSegment(sketch, "E54.bottom", {"start": v(123.45, 890.31) * mm, "end": v(300.57, 890.31) * mm});
            skLineSegment(sketch, "E54.top", {"start": v(123.45, 740.91) * mm, "end": v(300.57, 740.91) * mm});
            skLineSegment(sketch, "E54.left", {"start": v(123.45, 890.31) * mm, "end": v(123.45, 740.91) * mm});
            skLineSegment(sketch, "E54.right", {"start": v(300.57, 890.31) * mm, "end": v(300.57, 740.91) * mm});
            skLineSegment(sketch, "E55.bottom", {"start": v(124.2, 725.75) * mm, "end": v(301.25, 725.75) * mm});
            skLineSegment(sketch, "E55.top", {"start": v(124.2, 574.42) * mm, "end": v(301.25, 574.42) * mm});
            skLineSegment(sketch, "E55.left", {"start": v(124.2, 725.75) * mm, "end": v(124.2, 574.42) * mm});
            skLineSegment(sketch, "E55.right", {"start": v(301.25, 725.75) * mm, "end": v(301.25, 574.42) * mm});
            skLineSegment(sketch, "E56.bottom", {"start": v(124.2, 555.3) * mm, "end": v(298.25, 555.3) * mm});
            skLineSegment(sketch, "E56.top", {"start": v(124.2, 403.8) * mm, "end": v(298.25, 403.8) * mm});
            skLineSegment(sketch, "E56.left", {"start": v(124.2, 555.3) * mm, "end": v(124.2, 403.8) * mm});
            skLineSegment(sketch, "E56.right", {"start": v(298.25, 555.3) * mm, "end": v(298.25, 403.8) * mm});
            skLineSegment(sketch, "E57.bottom", {"start": v(123.45, 1240.7) * mm, "end": v(297.87, 1240.7) * mm});
            skLineSegment(sketch, "E57.top", {"start": v(123.45, 1406.67) * mm, "end": v(297.87, 1406.67) * mm});
            skLineSegment(sketch, "E57.left", {"start": v(123.45, 1240.7) * mm, "end": v(123.45, 1406.67) * mm});
            skLineSegment(sketch, "E57.right", {"start": v(297.87, 1240.7) * mm, "end": v(297.87, 1406.67) * mm});
            skSolve(sketch);
        }
        {
            var Q0;
            Q0 = qSketchRegion(id + "F48", true);
            extrude(context, id + "F49", {"entities" : qUnion([Q0]), "operationType" : NewBodyOperationType.ADD, "depth" : 330.2 * mm, "offsetDistance" : 25.4 * mm});
        }
    });
